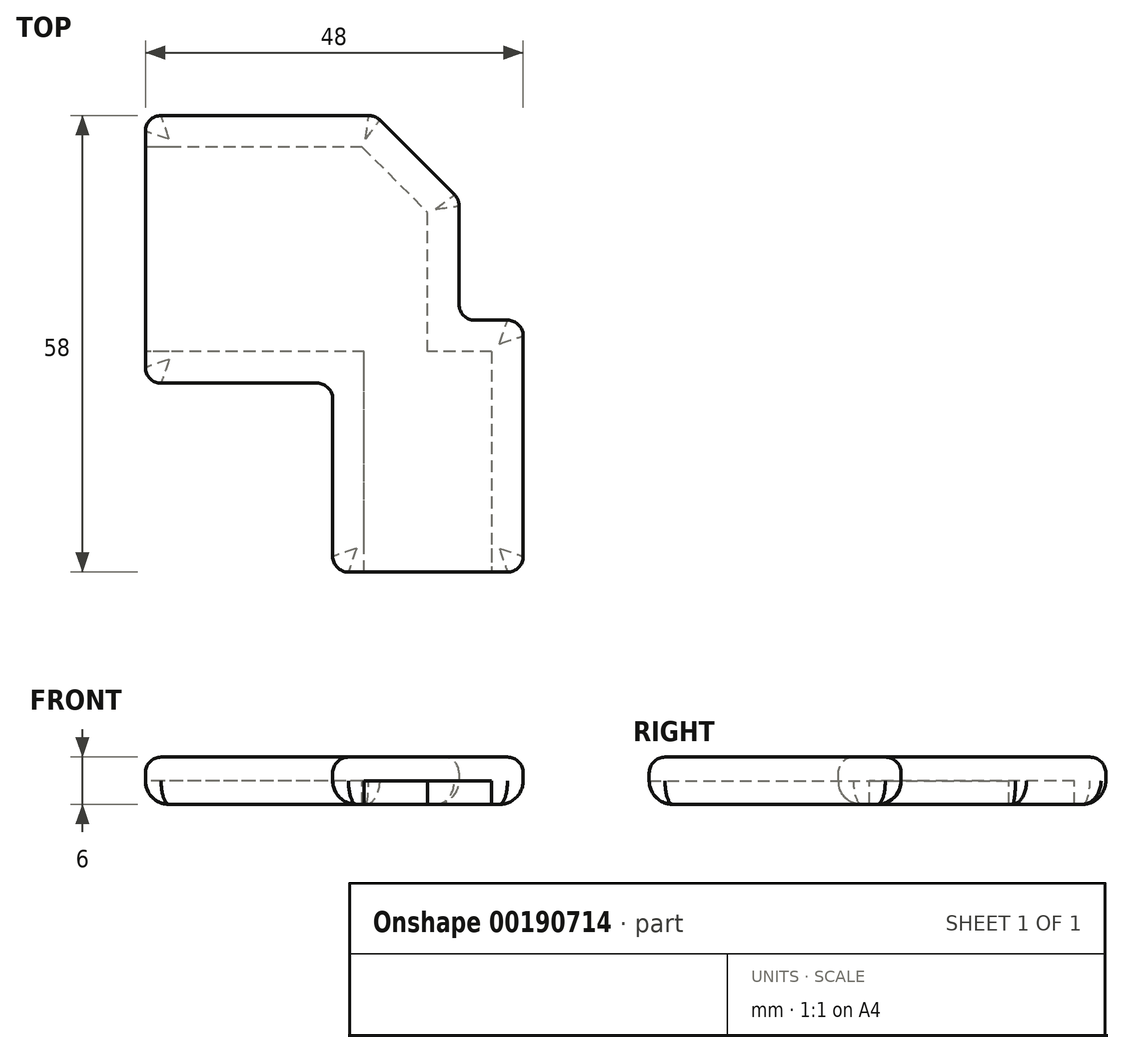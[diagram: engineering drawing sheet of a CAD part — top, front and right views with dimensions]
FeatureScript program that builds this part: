
annotation { "Feature Type Name" : "Feature", "Feature Type Description" : "" }
export const myFeature = defineFeature(function(context is Context, id is Id, definition is map)
    precondition{}
    {
        {
            var Q0;
            Q0=qCreatedBy(makeId("Top.planeOp"),FACE);
            var sketch = newSketch(context, id + "F0", { "sketchPlane" : qUnion([Q0])});
            skLineSegment(sketch, "E0.bottom", {"start": v(-16.45, 0) * mm, "end": v(-40, 0) * mm, "construction": true});
            skLineSegment(sketch, "E0.top", {"start": v(0, -26) * mm, "end": v(-8.15, -26) * mm, "construction": true});
            skLineSegment(sketch, "E0.right", {"start": v(-40, 0) * mm, "end": v(-40, -26) * mm, "construction": true});
            skLineSegment(sketch, "E1", {"start": v(-8.15, -26) * mm, "end": v(-8.15, -8.3) * mm, "construction": true});
            skLineSegment(sketch, "E2", {"start": v(0, -26) * mm, "end": v(0, -50) * mm, "construction": true});
            skLineSegment(sketch, "E3", {"start": v(0, -50) * mm, "end": v(-16.2, -50) * mm, "construction": true});
            skLineSegment(sketch, "E4", {"start": v(-16.2, -50) * mm, "end": v(-16.2, -26) * mm, "construction": true});
            skLineSegment(sketch, "E5.trimOffspring", {"start": v(-16.2, -26) * mm, "end": v(-40, -26) * mm, "construction": true});
            skLineSegment(sketch, "E6", {"start": v(-16.45, 0) * mm, "end": v(-8.15, -8.3) * mm, "construction": true});
            skLineSegment(sketch, "E7.0", {"start": v(2, -54) * mm, "end": v(-18.2, -54) * mm});
            skLineSegment(sketch, "E7.1", {"start": v(4, -24) * mm, "end": v(4, -52) * mm});
            skLineSegment(sketch, "E7.2", {"start": v(-20.2, -52) * mm, "end": v(-20.2, -32) * mm});
            skLineSegment(sketch, "E7.3", {"start": v(2, -22) * mm, "end": v(-2.15, -22) * mm});
            skLineSegment(sketch, "E7.4", {"start": v(-4.15, -20) * mm, "end": v(-4.15, -7.47) * mm});
            skLineSegment(sketch, "E7.5", {"start": v(-22.2, -30) * mm, "end": v(-42, -30) * mm});
            skLineSegment(sketch, "E7.6", {"start": v(-44, 2) * mm, "end": v(-44, -28) * mm});
            skLineSegment(sketch, "E7.7", {"start": v(-15.62, 4) * mm, "end": v(-42, 4) * mm});
            skLineSegment(sketch, "E7.8", {"start": v(-14.2, 3.41) * mm, "end": v(-4.74, -6.06) * mm});
            skPoint(sketch, "E8.visualSharp", {"position": v(-44, 4) * mm});
            skArc(sketch, "E8.filletArc", {"start": v(-42, 4) * mm, "mid": v(-43.41, 3.41) * mm, "end": v(-44, 2) * mm});
            skPoint(sketch, "E9.visualSharp", {"position": v(-14.8, 4) * mm});
            skArc(sketch, "E9.filletArc", {"start": v(-14.2, 3.41) * mm, "mid": v(-14.86, 3.85) * mm, "end": v(-15.62, 4) * mm});
            skPoint(sketch, "E10.visualSharp", {"position": v(-4.15, -6.64) * mm});
            skArc(sketch, "E10.filletArc", {"start": v(-4.15, -7.47) * mm, "mid": v(-4.3, -6.7) * mm, "end": v(-4.74, -6.06) * mm});
            skPoint(sketch, "E11.visualSharp", {"position": v(-4.15, -22) * mm});
            skArc(sketch, "E11.filletArc", {"start": v(-4.15, -20) * mm, "mid": v(-3.57, -21.41) * mm, "end": v(-2.15, -22) * mm});
            skPoint(sketch, "E12.visualSharp", {"position": v(4, -22) * mm});
            skArc(sketch, "E12.filletArc", {"start": v(4, -24) * mm, "mid": v(3.41, -22.59) * mm, "end": v(2, -22) * mm});
            skPoint(sketch, "E13.visualSharp", {"position": v(4, -54) * mm});
            skArc(sketch, "E13.filletArc", {"start": v(2, -54) * mm, "mid": v(3.41, -53.41) * mm, "end": v(4, -52) * mm});
            skPoint(sketch, "E14.visualSharp", {"position": v(-20.2, -54) * mm});
            skArc(sketch, "E14.filletArc", {"start": v(-20.2, -52) * mm, "mid": v(-19.61, -53.41) * mm, "end": v(-18.2, -54) * mm});
            skPoint(sketch, "E15.visualSharp", {"position": v(-20.2, -30) * mm});
            skArc(sketch, "E15.filletArc", {"start": v(-20.2, -32) * mm, "mid": v(-20.79, -30.59) * mm, "end": v(-22.2, -30) * mm});
            skPoint(sketch, "E16.visualSharp", {"position": v(-44, -30) * mm});
            skArc(sketch, "E16.filletArc", {"start": v(-44, -28) * mm, "mid": v(-43.41, -29.41) * mm, "end": v(-42, -30) * mm});
            skSolve(sketch);
        }
        {
            var Q0;
            Q0 = qSketchRegion(id + "F0", true);
            extrude(context, id + "F1", {"entities" : qUnion([Q0]), "depth" : 6 * mm, "symmetric" : true});
        }
        {
            var Q0;
            Q0=qCreatedBy(makeId("Top.planeOp"),FACE);
            var sketch = newSketch(context, id + "F2", { "sketchPlane" : qUnion([Q0])});
            skLineSegment(sketch, "E17.0", {"start": v(-16.45, 0) * mm, "end": v(-8.15, -8.3) * mm});
            skLineSegment(sketch, "E18.0", {"start": v(-8.15, -26) * mm, "end": v(-8.15, -8.3) * mm});
            skPoint(sketch, "E19.0", {"position": v(-4.08, -26) * mm});
            skLineSegment(sketch, "E20.0", {"start": v(0, -26) * mm, "end": v(-8.15, -26) * mm});
            skLineSegment(sketch, "E21.0", {"start": v(0, -26) * mm, "end": v(0, -54) * mm});
            skLineSegment(sketch, "E22.0", {"start": v(-16.2, -54) * mm, "end": v(-16.2, -26) * mm});
            skLineSegment(sketch, "E23.0", {"start": v(-16.2, -26) * mm, "end": v(-44, -26) * mm});
            skLineSegment(sketch, "E24.0", {"start": v(-16.45, 0) * mm, "end": v(-44, 0) * mm});
            skPoint(sketch, "E25.orphan", {"position": v(-40, 0) * mm});
            skPoint(sketch, "E26.orphan", {"position": v(-40, -26) * mm});
            skPoint(sketch, "E27.orphan", {"position": v(-16.2, -50) * mm});
            skPoint(sketch, "E28.0.start.orphan", {"position": v(0, -50) * mm});
            skLineSegment(sketch, "E29.0", {"start": v(0, -54) * mm, "end": v(-16.2, -54) * mm});
            skLineSegment(sketch, "E30.0", {"start": v(-44, 0) * mm, "end": v(-44, -26) * mm});
            skPoint(sketch, "E31.orphan", {"position": v(-44, 2) * mm});
            skPoint(sketch, "E32.orphan", {"position": v(-44, -28) * mm});
            skPoint(sketch, "E33.orphan", {"position": v(-18.2, -54) * mm});
            skPoint(sketch, "E34.orphan", {"position": v(2, -54) * mm});
            skSolve(sketch);
        }
        {
            var Q0;
            Q0 = qSketchRegion(id + "F2", true);
            extrude(context, id + "F3", {"entities" : qUnion([Q0]), "operationType" : NewBodyOperationType.REMOVE, "oppositeDirection" : true, "depth" : 4 * mm});
        }
        {
            var Q0;
            Q0=makeQuery(id+"F1.opExtrude","CAP_EDGE",EDGE,{"disambiguationData":[OSD([sQuery(id+"F0.wireOp",EDGE,"E7.5")])],"isStart":true});
            var Q1;
            Q1=makeQuery(id+"F1.opExtrude","CAP_EDGE",EDGE,{"disambiguationData":[OSD([sQuery(id+"F0.wireOp",EDGE,"E7.1")])],"isStart":true});
            fillet(context, id + "F4", {"entities" : qUnion([Q0, Q1]), "radius" : 3 * mm, "tangentPropagation" : true, "allowEdgeOverflow" : false});
        }
        {
            var Q0;
            Q0=makeQuery(id+"F1.opExtrude","CAP_EDGE",EDGE,{"disambiguationData":[OSD([sQuery(id+"F0.wireOp",EDGE,"E7.1")])],"isStart":false});
            fillet(context, id + "F5", {"entities" : qUnion([Q0]), "radius" : 2 * mm, "tangentPropagation" : true, "allowEdgeOverflow" : false});
        }
    });
